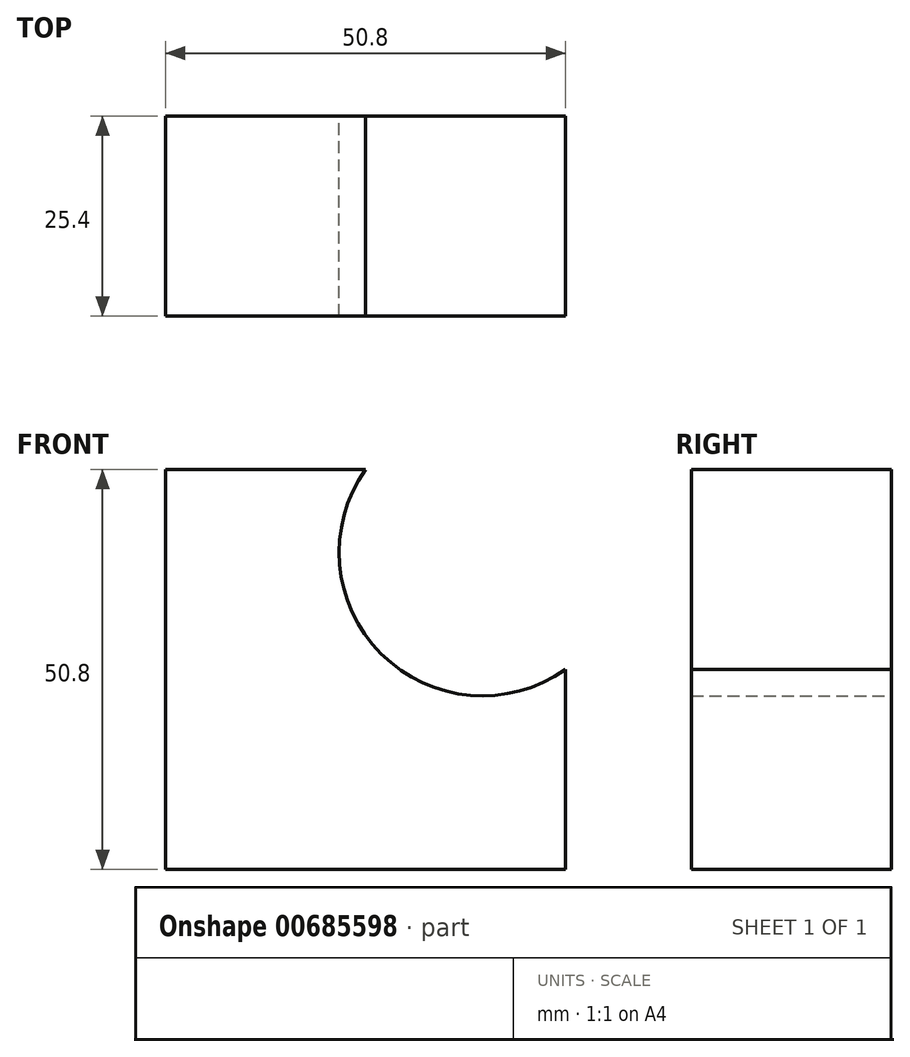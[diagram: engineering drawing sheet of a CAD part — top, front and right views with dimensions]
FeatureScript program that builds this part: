
annotation { "Feature Type Name" : "Feature", "Feature Type Description" : "" }
export const myFeature = defineFeature(function(context is Context, id is Id, definition is map)
    precondition{}
    {
        {
            var Q0;
            Q0=qCreatedBy(makeId("Front.planeOp"),FACE);
            var sketch = newSketch(context, id + "F0", { "sketchPlane" : qUnion([Q0])});
            skLineSegment(sketch, "E0", {"start": v(0, 50.8) * mm, "end": v(0, 0) * mm});
            skLineSegment(sketch, "E1", {"start": v(0, 0) * mm, "end": v(50.8, 0) * mm});
            skLineSegment(sketch, "E2", {"start": v(50.8, 0) * mm, "end": v(50.8, 25.4) * mm});
            skLineSegment(sketch, "E3", {"start": v(0, 50.8) * mm, "end": v(25.4, 50.8) * mm});
            skArc(sketch, "E4", {"start": v(25.4, 50.8) * mm, "mid": v(27.4, 27.4) * mm, "end": v(50.8, 25.4) * mm});
            skSolve(sketch);
        }
        {
            var Q0;
            Q0 = qSketchRegion(id + "F0", true);
            extrude(context, id + "F1", {"entities" : qUnion([Q0]), "depth" : 25.4 * mm, "offsetDistance" : 25.4 * mm});
        }
    });
